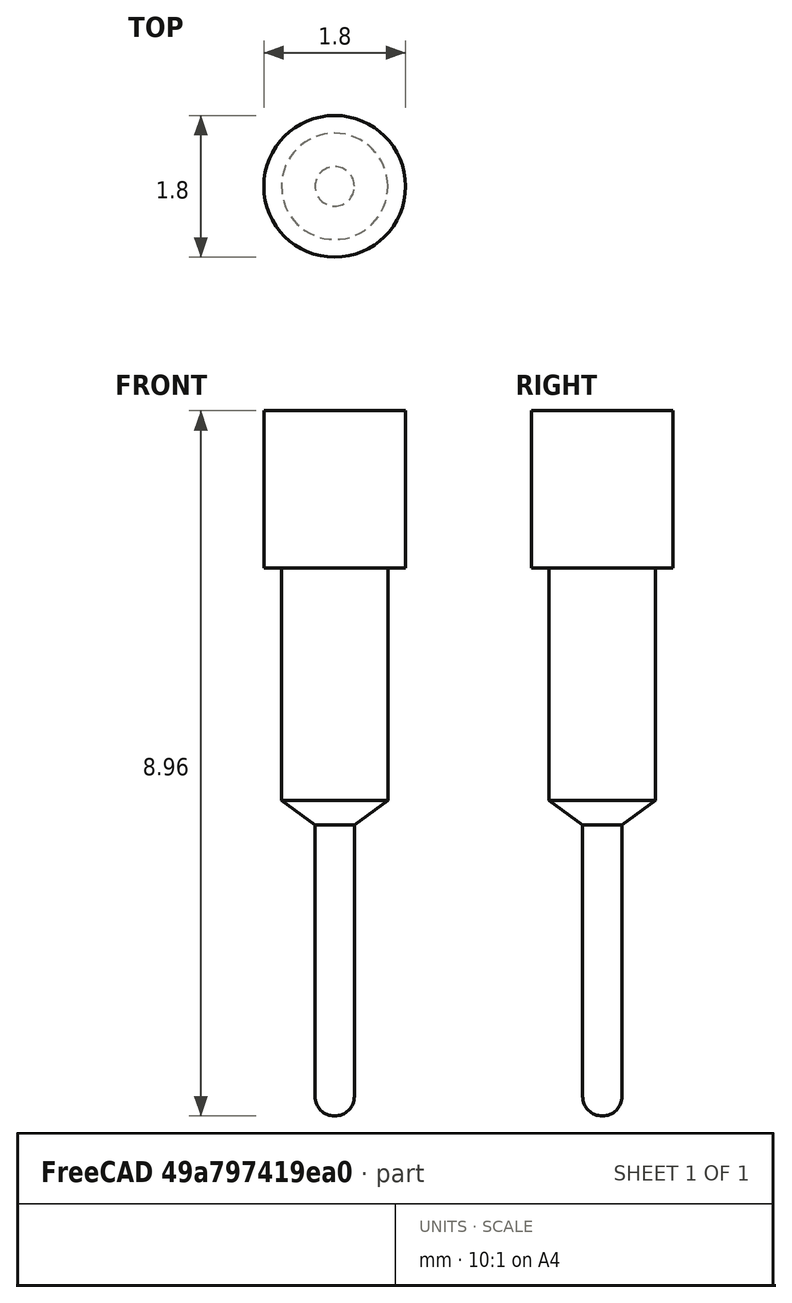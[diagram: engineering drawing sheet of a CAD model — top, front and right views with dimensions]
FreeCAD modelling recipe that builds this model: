
FCSTD DOCUMENT  (FreeCAD 0.21R33771 (Git))
Label: Connfly_DS-1006-11_No_Pin
License: All rights reserved
LicenseURL: https://en.wikipedia.org/wiki/All_rights_reserved
objects: Sketcher::SketchObject×1, PartDesign::Revolution×1, PartDesign::Body×1
note: 4 computed .brp shape members not serialized (recipe doc carries the construction recipe); baked Part::Feature solids carry a one-line shape summary decoded from their .brp

FEATURE [Sketcher::SketchObject] Sketch
  FullyConstrained = true
  MapMode = 5
  Placement = pos=(0,0,0) rot=(1,0,0;1.5708rad)
  Support = -> [XZ_Plane]
  sketch-geometry (10):
    g0: LineSegment StartX=0 StartY=8.26 StartZ=0 EndX=0 EndY=-3.7 EndZ=0
    g1: LineSegment StartX=0 StartY=5.26 StartZ=0 EndX=-0.9 EndY=5.26 EndZ=0
    g2: LineSegment StartX=-0.9 StartY=5.26 StartZ=0 EndX=-0.9 EndY=3.26 EndZ=0
    g3: LineSegment StartX=-0.9 StartY=3.26 StartZ=0 EndX=-0.675 EndY=3.26 EndZ=0
    g4: LineSegment StartX=-0.675 StartY=3.26 StartZ=0 EndX=-0.675 EndY=0.31 EndZ=0
    g5: LineSegment StartX=-0.675 StartY=0.31 StartZ=0 EndX=-0.25 EndY=0 EndZ=0
    g6: LineSegment StartX=-0.25 StartY=0 StartZ=0 EndX=-0.25 EndY=-3.45 EndZ=0
    g7: ArcOfCircle CenterX=0 CenterY=-3.45 CenterZ=0 NormalX=0 NormalY=0 NormalZ=1 AngleXU=0 Radius=0.25 StartAngle=3.14159 EndAngle=4.71239
    g8: GeomPoint X=0 Y=0 Z=0
    g9: LineSegment StartX=0 StartY=5.26 StartZ=0 EndX=0 EndY=-3.7 EndZ=0
  constraints (29):
    c: Vertical(g0)
    c: Horizontal(g1)
    c: Coincident(g1,g2)
    c: Vertical(g2)
    c: Coincident(g2,g3)
    c: Coincident(g3,g4)
    c: Vertical(g4)
    c: Coincident(g4,g5)
    c: Coincident(g5,g6)
    c: Vertical(g6)
    c: Coincident(g7,g6)
    c: Horizontal(g3)
    c: Vertical(g7,g0)
    c: Angle(g7) = 1.5708
    c: DistanceX(g6,g7) = 0.25
    c: DistanceY(g1,g0) = 3
    c: DistanceY(g2,g0) = 5
    c: DistanceY(g4,g0) = 7.95
    c: DistanceY(g5,g0) = 8.26
    c: DistanceY(g0,g0) = 11.96
    c: DistanceX(g1,g0) = 0.9
    c: DistanceX(g3,g0) = 0.675
    c: Coincident(g0,g7)
    c: PointOnObject(g8,g0)
    c: Horizontal(g8,g5)
    c: Coincident(g8,g-1)
    c: PointOnObject(g1,g0)
    c: Coincident(g9,g1)
    c: Coincident(g9,g7)
FEATURE [PartDesign::Revolution] Revolution
  Angle = 360
  Axis = (0,-2e-16,1)
  Base = (0,0,0)
  Placement = pos=(0,0,0) rot=(1,0,0;1.5708rad)
  Profile = -> Sketch
  ReferenceAxis = -> Sketch [V_Axis]
FEATURE [PartDesign::Body] Body
  Group = -> [Sketch,Revolution]
  Origin = -> Origin
  Tip = -> Revolution
